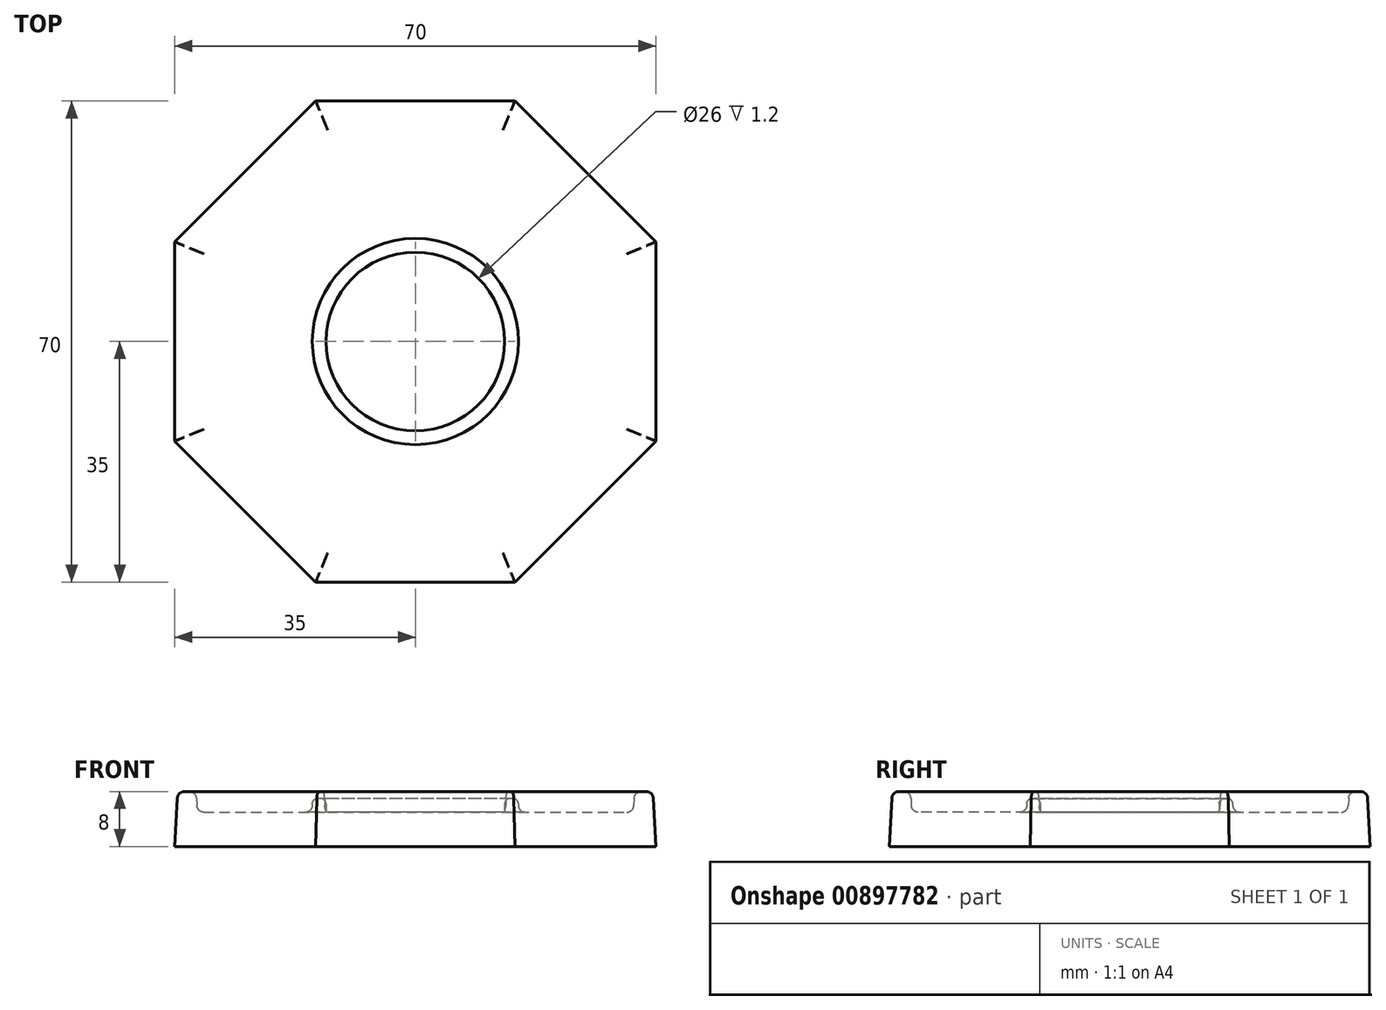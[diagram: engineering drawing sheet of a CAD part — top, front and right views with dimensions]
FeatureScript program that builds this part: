
annotation { "Feature Type Name" : "Feature", "Feature Type Description" : "" }
export const myFeature = defineFeature(function(context is Context, id is Id, definition is map)
    precondition{}
    {
        {
            var Q0;
            Q0=qCreatedBy(makeId("Top.planeOp"),FACE);
            var sketch = newSketch(context, id + "F0", { "sketchPlane" : qUnion([Q0])});
            skCircle(sketch, "E0.cCircle", {"center": v(0, 0) * mm, "radius": 37.88 * mm, "construction": true});
            skLineSegment(sketch, "E0.0", {"start": v(14.5, 35) * mm, "end": v(35, 14.5) * mm});
            skLineSegment(sketch, "E0.1", {"start": v(35, 14.5) * mm, "end": v(35, -14.5) * mm});
            skLineSegment(sketch, "E0.2", {"start": v(35, -14.5) * mm, "end": v(14.5, -35) * mm});
            skLineSegment(sketch, "E0.3", {"start": v(14.5, -35) * mm, "end": v(-14.5, -35) * mm});
            skLineSegment(sketch, "E0.4", {"start": v(-14.5, -35) * mm, "end": v(-35, -14.5) * mm});
            skLineSegment(sketch, "E0.5", {"start": v(-35, -14.5) * mm, "end": v(-35, 14.5) * mm});
            skLineSegment(sketch, "E0.6", {"start": v(-35, 14.5) * mm, "end": v(-14.5, 35) * mm});
            skLineSegment(sketch, "E0.7", {"start": v(-14.5, 35) * mm, "end": v(14.5, 35) * mm});
            skSolve(sketch);
        }
        {
            var Q0;
            Q0 = qSketchRegion(id + "F0", true);
            extrude(context, id + "F1", {"entities" : qUnion([Q0]), "depth" : 5 * mm, "offsetDistance" : 25 * mm, "hasDraft" : true, "draftAngle" : 3 * degree, "draftPullDirection" : true});
        }
        {
            var Q0;
            Q0=makeQuery(id+"F1.opExtrude","CAP_FACE",FACE,{"disambiguationData":[OSD([sQuery(id+"F0.wireOp",EDGE,"E0.0"),sQuery(id+"F0.wireOp",EDGE,"E0.1"),sQuery(id+"F0.wireOp",EDGE,"E0.2"),sQuery(id+"F0.wireOp",EDGE,"E0.3"),sQuery(id+"F0.wireOp",EDGE,"E0.4"),sQuery(id+"F0.wireOp",EDGE,"E0.5"),sQuery(id+"F0.wireOp",EDGE,"E0.6"),sQuery(id+"F0.wireOp",EDGE,"E0.7")])],"isStart":false});
            var sketch = newSketch(context, id + "F2", { "sketchPlane" : qUnion([Q0])});
            skLineSegment(sketch, "E1.0", {"start": v(31.74, 13.15) * mm, "end": v(13.15, 31.74) * mm});
            skLineSegment(sketch, "E1.1", {"start": v(31.74, -13.15) * mm, "end": v(31.74, 13.15) * mm});
            skLineSegment(sketch, "E1.2", {"start": v(13.15, 31.74) * mm, "end": v(-13.15, 31.74) * mm});
            skLineSegment(sketch, "E1.3", {"start": v(13.15, -31.74) * mm, "end": v(31.74, -13.15) * mm});
            skLineSegment(sketch, "E1.4", {"start": v(-13.15, 31.74) * mm, "end": v(-31.74, 13.15) * mm});
            skLineSegment(sketch, "E1.5", {"start": v(-31.74, 13.15) * mm, "end": v(-31.74, -13.15) * mm});
            skLineSegment(sketch, "E1.6", {"start": v(-31.74, -13.15) * mm, "end": v(-13.15, -31.74) * mm});
            skLineSegment(sketch, "E1.7", {"start": v(-13.15, -31.74) * mm, "end": v(13.15, -31.74) * mm});
            skLineSegment(sketch, "E2.0.0", {"start": v(14.39, 34.74) * mm, "end": v(-14.39, 34.74) * mm});
            skLineSegment(sketch, "E2.0.1", {"start": v(-14.39, 34.74) * mm, "end": v(-34.74, 14.39) * mm});
            skLineSegment(sketch, "E2.0.2", {"start": v(-34.74, 14.39) * mm, "end": v(-34.74, -14.39) * mm});
            skLineSegment(sketch, "E2.0.3", {"start": v(-34.74, -14.39) * mm, "end": v(-14.39, -34.74) * mm});
            skLineSegment(sketch, "E2.0.4", {"start": v(-14.39, -34.74) * mm, "end": v(14.39, -34.74) * mm});
            skLineSegment(sketch, "E2.0.5", {"start": v(14.39, -34.74) * mm, "end": v(34.74, -14.39) * mm});
            skLineSegment(sketch, "E2.0.6", {"start": v(34.74, -14.39) * mm, "end": v(34.74, 14.39) * mm});
            skLineSegment(sketch, "E2.0.7", {"start": v(34.74, 14.39) * mm, "end": v(14.39, 34.74) * mm});
            skSolve(sketch);
        }
        {
            var Q0;
            Q0 = qSketchRegion(id + "F2", true);
            extrude(context, id + "F3", {"entities" : qUnion([Q0]), "operationType" : NewBodyOperationType.ADD, "depth" : 3 * mm, "offsetDistance" : 25 * mm, "hasDraft" : true, "draftAngle" : 3 * degree, "draftPullDirection" : true});
        }
        {
            var Q0;
            Q0=makeQuery(id+"F3.opExtrude","CAP_EDGE",EDGE,{"disambiguationData":[OSD([sQuery(id+"F2.wireOp",EDGE,"E2.0.4")])],"isStart":false});
            var Q1;
            Q1=makeQuery(id+"F3.opExtrude","CAP_EDGE",EDGE,{"disambiguationData":[OSD([sQuery(id+"F2.wireOp",EDGE,"E2.0.3")])],"isStart":false});
            var Q2;
            Q2=makeQuery(id+"F3.opExtrude","CAP_EDGE",EDGE,{"disambiguationData":[OSD([sQuery(id+"F2.wireOp",EDGE,"E2.0.5")])],"isStart":false});
            var Q3;
            Q3=makeQuery(id+"F3.opExtrude","CAP_EDGE",EDGE,{"disambiguationData":[OSD([sQuery(id+"F2.wireOp",EDGE,"E2.0.6")])],"isStart":false});
            var Q4;
            Q4=makeQuery(id+"F3.opExtrude","CAP_EDGE",EDGE,{"disambiguationData":[OSD([sQuery(id+"F2.wireOp",EDGE,"E2.0.7")])],"isStart":false});
            var Q5;
            Q5=makeQuery(id+"F3.opExtrude","CAP_EDGE",EDGE,{"disambiguationData":[OSD([sQuery(id+"F2.wireOp",EDGE,"E1.2")])],"isStart":false});
            var Q6;
            Q6=makeQuery(id+"F3.opExtrude","CAP_EDGE",EDGE,{"disambiguationData":[OSD([sQuery(id+"F2.wireOp",EDGE,"E2.0.0")])],"isStart":false});
            var Q7;
            Q7=makeQuery(id+"F3.opExtrude","CAP_EDGE",EDGE,{"disambiguationData":[OSD([sQuery(id+"F2.wireOp",EDGE,"E2.0.1")])],"isStart":false});
            var Q8;
            Q8=makeQuery(id+"F3.opExtrude","CAP_EDGE",EDGE,{"disambiguationData":[OSD([sQuery(id+"F2.wireOp",EDGE,"E2.0.2")])],"isStart":false});
            var Q9;
            Q9=makeQuery(id+"F3.opExtrude","CAP_EDGE",EDGE,{"disambiguationData":[OSD([sQuery(id+"F2.wireOp",EDGE,"E1.4")])],"isStart":false});
            var Q10;
            Q10=makeQuery(id+"F3.opExtrude","CAP_EDGE",EDGE,{"disambiguationData":[OSD([sQuery(id+"F2.wireOp",EDGE,"E1.5")])],"isStart":false});
            var Q11;
            Q11=makeQuery(id+"F3.opExtrude","CAP_EDGE",EDGE,{"disambiguationData":[OSD([sQuery(id+"F2.wireOp",EDGE,"E1.6")])],"isStart":false});
            var Q12;
            Q12=makeQuery(id+"F3.opExtrude","CAP_EDGE",EDGE,{"disambiguationData":[OSD([sQuery(id+"F2.wireOp",EDGE,"E1.7")])],"isStart":false});
            var Q13;
            Q13=makeQuery(id+"F3.opExtrude","CAP_EDGE",EDGE,{"disambiguationData":[OSD([sQuery(id+"F2.wireOp",EDGE,"E1.3")])],"isStart":false});
            var Q14;
            Q14=makeQuery(id+"F3.opExtrude","CAP_EDGE",EDGE,{"disambiguationData":[OSD([sQuery(id+"F2.wireOp",EDGE,"E1.1")])],"isStart":false});
            var Q15;
            Q15=makeQuery(id+"F3.opExtrude","CAP_EDGE",EDGE,{"disambiguationData":[OSD([sQuery(id+"F2.wireOp",EDGE,"E1.0")])],"isStart":false});
            fillet(context, id + "F4", {"entities" : qUnion([Q0, Q1, Q2, Q3, Q4, Q5, Q6, Q7, Q8, Q9, Q10, Q11, Q12, Q13, Q14, Q15]), "radius" : 1 * mm, "tangentPropagation" : true, "allowEdgeOverflow" : false});
        }
        {
            var Q0;
            Q0=makeQuery(id+"F1.opExtrude","CAP_FACE",FACE,{"disambiguationData":[OSD([sQuery(id+"F0.wireOp",EDGE,"E0.0"),sQuery(id+"F0.wireOp",EDGE,"E0.1"),sQuery(id+"F0.wireOp",EDGE,"E0.2"),sQuery(id+"F0.wireOp",EDGE,"E0.3"),sQuery(id+"F0.wireOp",EDGE,"E0.4"),sQuery(id+"F0.wireOp",EDGE,"E0.5"),sQuery(id+"F0.wireOp",EDGE,"E0.6"),sQuery(id+"F0.wireOp",EDGE,"E0.7")])],"isStart":false});
            var sketch = newSketch(context, id + "F5", { "sketchPlane" : qUnion([Q0])});
            skCircle(sketch, "E3", {"center": v(0, 0) * mm, "radius": 15 * mm});
            skCircle(sketch, "E4", {"center": v(0, 0) * mm, "radius": 13 * mm});
            skSolve(sketch);
        }
        {
            var Q0;
            Q0 = qSketchRegion(id + "F5", true);
            extrude(context, id + "F6", {"entities" : qUnion([Q0]), "operationType" : NewBodyOperationType.ADD, "depth" : 2 * mm, "offsetDistance" : 25 * mm});
        }
        {
            var Q0;
            Q0=makeQuery(id+"F6.opExtrude","CAP_EDGE",EDGE,{"disambiguationData":[OSD([sQuery(id+"F5.wireOp",EDGE,"E3")])],"isStart":false});
            var Q1;
            Q1=makeQuery(id+"F6.opExtrude","CAP_EDGE",EDGE,{"disambiguationData":[OSD([sQuery(id+"F5.wireOp",EDGE,"E4")])],"isStart":false});
            fillet(context, id + "F7", {"entities" : qUnion([Q0, Q1]), "radius" : 0.8 * mm, "tangentPropagation" : true, "allowEdgeOverflow" : false});
        }
        {
            var Q0;
            Q0=makeQuery(id+"F6.boolean.opBoolean","SPLIT",FACE,{"disambiguationData":[TD([makeQuery(id+"F3.opExtrude","SWEPT_FACE",FACE,{"disambiguationData":[OSD([sQuery(id+"F2.wireOp",EDGE,"E1.0")])]})])],"derivedFrom":makeQuery(id+"F1.opExtrude","CAP_FACE",FACE,{"disambiguationData":[OSD([sQuery(id+"F0.wireOp",EDGE,"E0.0"),sQuery(id+"F0.wireOp",EDGE,"E0.1"),sQuery(id+"F0.wireOp",EDGE,"E0.2"),sQuery(id+"F0.wireOp",EDGE,"E0.3"),sQuery(id+"F0.wireOp",EDGE,"E0.4"),sQuery(id+"F0.wireOp",EDGE,"E0.5"),sQuery(id+"F0.wireOp",EDGE,"E0.6"),sQuery(id+"F0.wireOp",EDGE,"E0.7")])],"isStart":false})});
            fillet(context, id + "F8", {"entities" : qUnion([Q0]), "radius" : 1 * mm, "tangentPropagation" : true, "allowEdgeOverflow" : false});
        }
    });
